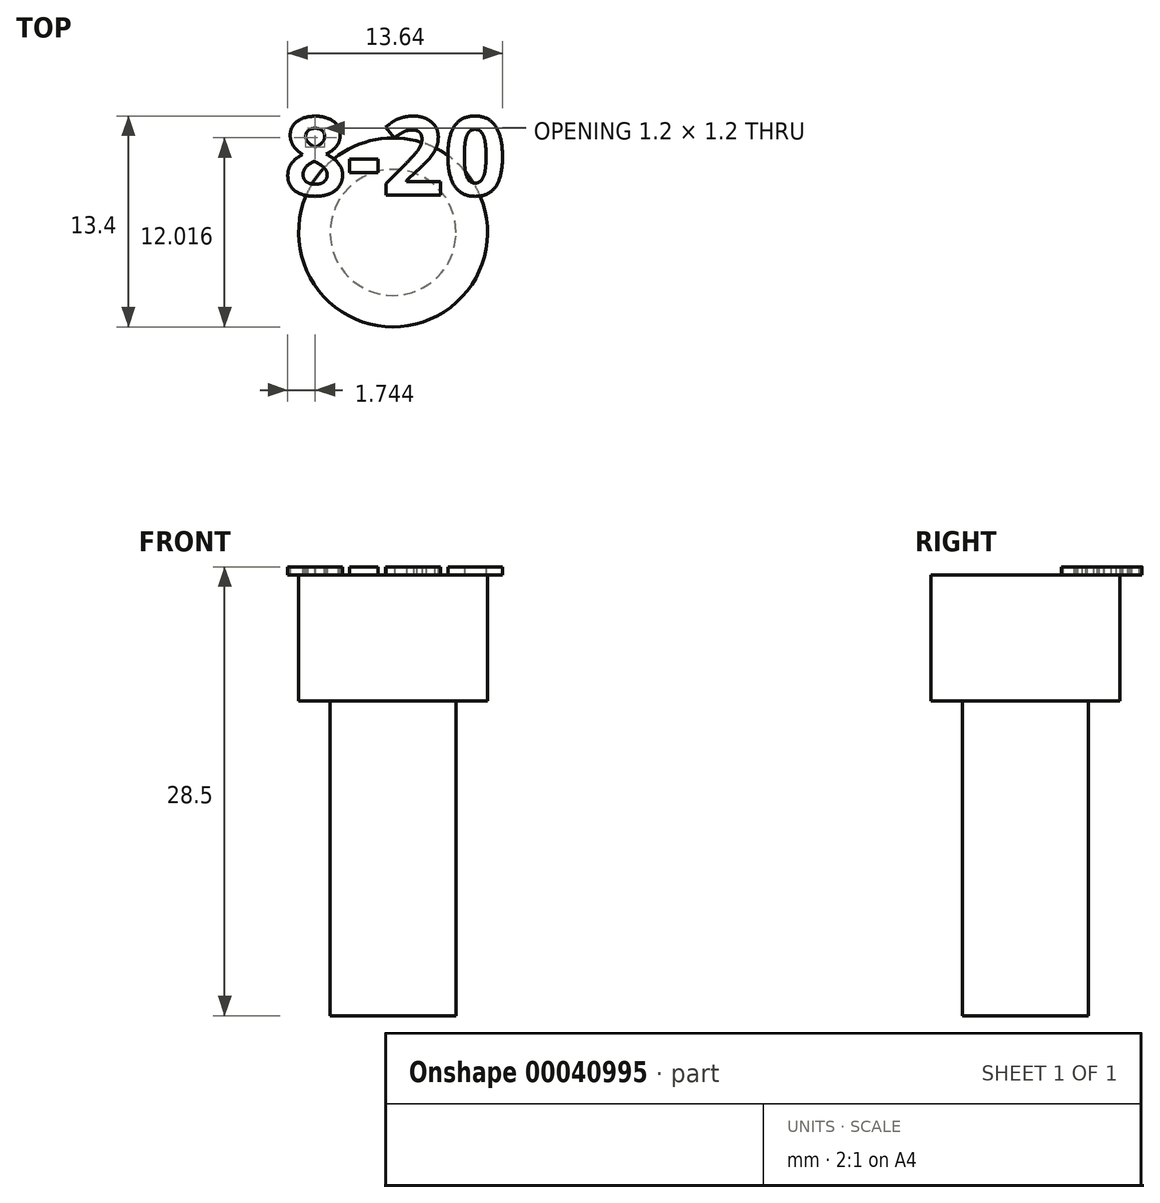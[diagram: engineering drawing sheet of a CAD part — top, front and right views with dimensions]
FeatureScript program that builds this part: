
annotation { "Feature Type Name" : "Feature", "Feature Type Description" : "" }
export const myFeature = defineFeature(function(context is Context, id is Id, definition is map)
    precondition{}
    {
        {
            var Q0;
            Q0=qCreatedBy(makeId("Top.planeOp"),FACE);
            var sketch = newSketch(context, id + "F0", { "sketchPlane" : qUnion([Q0])});
            skCircle(sketch, "E0", {"center": v(0, 0) * mm, "radius": 4 * mm});
            skSolve(sketch);
        }
        {
            var Q0;
            Q0=qSketchRegion(id+"F0",true);
            extrude(context, id + "F1", {"entities" : qUnion([Q0]), "depth" : 20 * mm});
        }
        {
            var Q0;
            Q0=makeQuery(id+"F1.opExtrude","CAP_FACE",FACE,{"disambiguationData":[OSD([sQuery(id+"F0.wireOp",EDGE,"E0")])],"isStart":false});
            var sketch = newSketch(context, id + "F2", { "sketchPlane" : qUnion([Q0])});
            skCircle(sketch, "E1", {"center": v(0, 0) * mm, "radius": 6 * mm});
            skSolve(sketch);
        }
        {
            var Q0;
            Q0=qSketchRegion(id+"F2",true);
            extrude(context, id + "F3", {"entities" : qUnion([Q0]), "operationType" : NewBodyOperationType.ADD, "depth" : 8 * mm});
        }
        {
            var Q0;
            Q0=makeQuery(id+"F3.opExtrude","CAP_FACE",FACE,{"disambiguationData":[OSD([sQuery(id+"F2.wireOp",EDGE,"E1")])],"isStart":false});
            var sketch = newSketch(context, id + "F4", { "sketchPlane" : qUnion([Q0])});
            skText(sketch, "E2", { "text": "8-20", "fontName": "OpenSans-Bold.ttf"});
            const initialGuessF4  = {"E2": [-0.00693, 0.00236, 1, 0, 0.005]};
            skSetInitialGuess(sketch, initialGuessF4);
            skSolve(sketch);
        }
        {
            var Q0;
            Q0=qSketchRegion(id+"F4",true);
            extrude(context, id + "F5", {"entities" : qUnion([Q0]), "operationType" : NewBodyOperationType.ADD, "depth" : 0.5 * mm});
        }
    });
